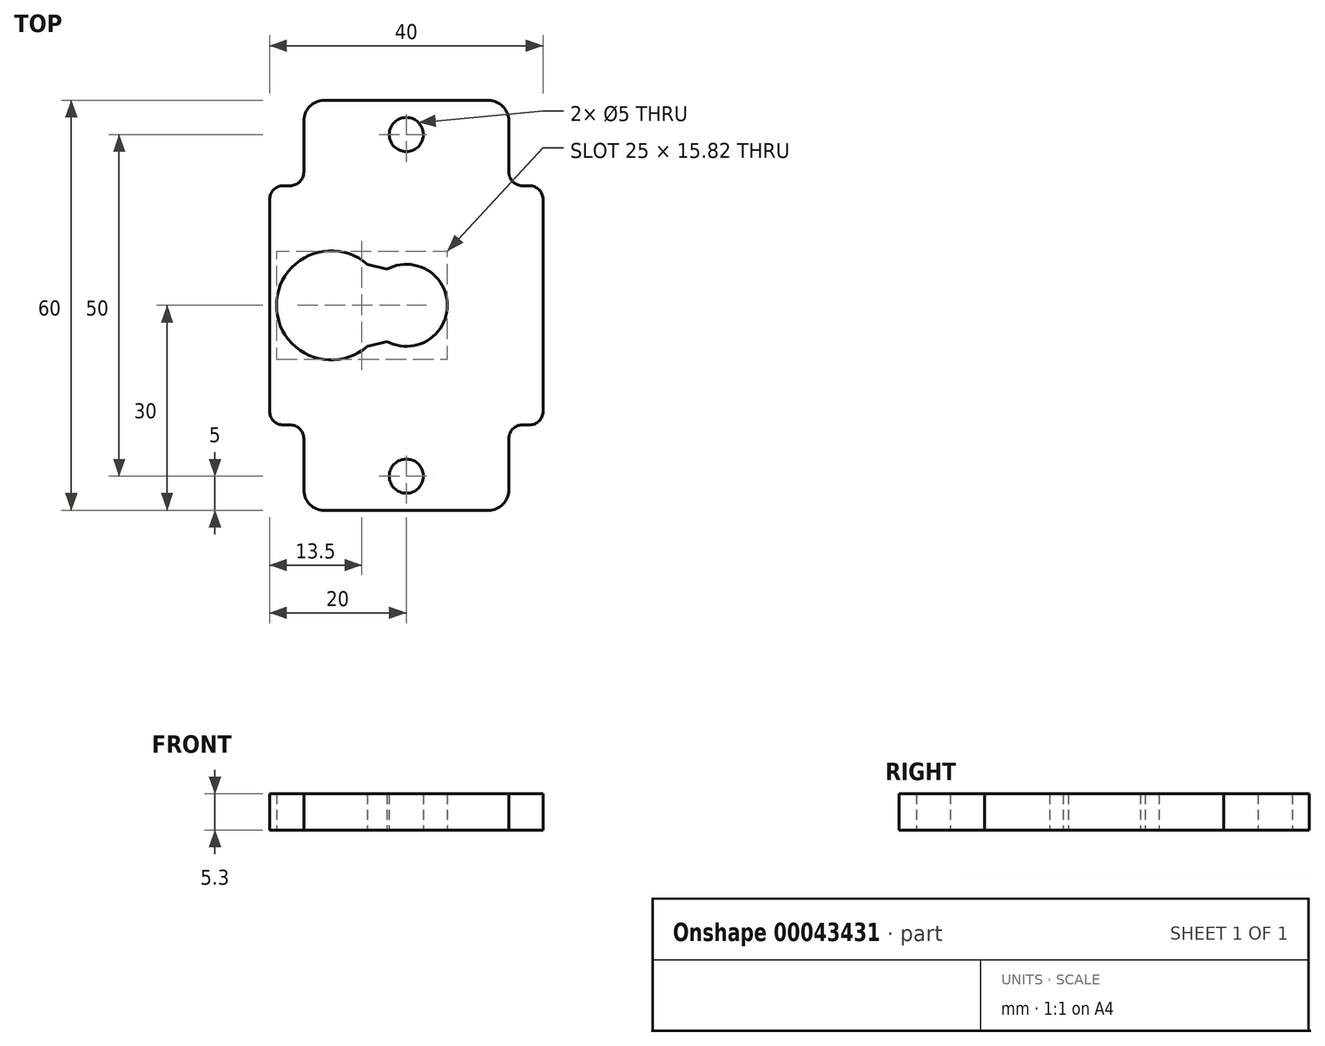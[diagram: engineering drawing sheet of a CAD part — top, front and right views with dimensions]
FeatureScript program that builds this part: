
annotation { "Feature Type Name" : "Feature", "Feature Type Description" : "" }
export const myFeature = defineFeature(function(context is Context, id is Id, definition is map)
    precondition{}
    {
        {
            var Q0;
            Q0=qCreatedBy(makeId("Top.planeOp"),FACE);
            var sketch = newSketch(context, id + "F0", { "sketchPlane" : qUnion([Q0])});
            skLineSegment(sketch, "E0.rect.bottom", {"start": v(12, -30) * mm, "end": v(-12, -30) * mm});
            skLineSegment(sketch, "E0.rect.top", {"start": v(12, 30) * mm, "end": v(-12, 30) * mm});
            skLineSegment(sketch, "E0.rect.left", {"start": v(15, -27) * mm, "end": v(15, -19.5) * mm});
            skLineSegment(sketch, "E0.rect.right", {"start": v(-15, -27) * mm, "end": v(-15, -19.5) * mm});
            skPoint(sketch, "E0.rect.middle", {"position": v(0, 0) * mm});
            skPoint(sketch, "E1.visualSharp", {"position": v(-15, 30) * mm});
            skArc(sketch, "E1.filletArc", {"start": v(-12, 30) * mm, "mid": v(-14.12, 29.12) * mm, "end": v(-15, 27) * mm});
            skPoint(sketch, "E2.visualSharp", {"position": v(15, 30) * mm});
            skArc(sketch, "E2.filletArc", {"start": v(15, 27) * mm, "mid": v(14.12, 29.12) * mm, "end": v(12, 30) * mm});
            skPoint(sketch, "E3.visualSharp", {"position": v(15, -30) * mm});
            skArc(sketch, "E3.filletArc", {"start": v(12, -30) * mm, "mid": v(14.12, -29.12) * mm, "end": v(15, -27) * mm});
            skPoint(sketch, "E4.visualSharp", {"position": v(-15, -30) * mm});
            skArc(sketch, "E4.filletArc", {"start": v(-15, -27) * mm, "mid": v(-14.12, -29.12) * mm, "end": v(-12, -30) * mm});
            skLineSegment(sketch, "E5.rect.bottom", {"start": v(18, 17.5) * mm, "end": v(17, 17.5) * mm});
            skLineSegment(sketch, "E5.rect.top", {"start": v(18, -17.5) * mm, "end": v(17, -17.5) * mm});
            skLineSegment(sketch, "E5.rect.left", {"start": v(20, 15.5) * mm, "end": v(20, -15.5) * mm});
            skLineSegment(sketch, "E5.rect.right", {"start": v(-20, 15.5) * mm, "end": v(-20, -15.5) * mm});
            skLineSegment(sketch, "E6.trimOffspring", {"start": v(-17, 17.5) * mm, "end": v(-18, 17.5) * mm});
            skLineSegment(sketch, "E7.trimOffspring", {"start": v(-15, 19.5) * mm, "end": v(-15, 27) * mm});
            skLineSegment(sketch, "E8.trimOffspring", {"start": v(15, 19.5) * mm, "end": v(15, 27) * mm});
            skLineSegment(sketch, "E9.trimOffspring", {"start": v(-17, -17.5) * mm, "end": v(-18, -17.5) * mm});
            skPoint(sketch, "E10.visualSharp", {"position": v(-15, 17.5) * mm});
            skArc(sketch, "E10.filletArc", {"start": v(-17, 17.5) * mm, "mid": v(-15.59, 18.09) * mm, "end": v(-15, 19.5) * mm});
            skPoint(sketch, "E11.visualSharp", {"position": v(-20, 17.5) * mm});
            skArc(sketch, "E11.filletArc", {"start": v(-18, 17.5) * mm, "mid": v(-19.41, 16.91) * mm, "end": v(-20, 15.5) * mm});
            skPoint(sketch, "E12.visualSharp", {"position": v(-20, -17.5) * mm});
            skArc(sketch, "E12.filletArc", {"start": v(-20, -15.5) * mm, "mid": v(-19.41, -16.91) * mm, "end": v(-18, -17.5) * mm});
            skPoint(sketch, "E13.visualSharp", {"position": v(-15, -17.5) * mm});
            skArc(sketch, "E13.filletArc", {"start": v(-15, -19.5) * mm, "mid": v(-15.59, -18.09) * mm, "end": v(-17, -17.5) * mm});
            skPoint(sketch, "E14.visualSharp", {"position": v(15, -17.5) * mm});
            skArc(sketch, "E14.filletArc", {"start": v(17, -17.5) * mm, "mid": v(15.59, -18.09) * mm, "end": v(15, -19.5) * mm});
            skPoint(sketch, "E15.visualSharp", {"position": v(20, -17.5) * mm});
            skArc(sketch, "E15.filletArc", {"start": v(18, -17.5) * mm, "mid": v(19.41, -16.91) * mm, "end": v(20, -15.5) * mm});
            skPoint(sketch, "E16.visualSharp", {"position": v(20, 17.5) * mm});
            skArc(sketch, "E16.filletArc", {"start": v(20, 15.5) * mm, "mid": v(19.41, 16.91) * mm, "end": v(18, 17.5) * mm});
            skPoint(sketch, "E17.visualSharp", {"position": v(15, 17.5) * mm});
            skArc(sketch, "E17.filletArc", {"start": v(15, 19.5) * mm, "mid": v(15.59, 18.09) * mm, "end": v(17, 17.5) * mm});
            skArc(sketch, "E18", {"start": v(-5.7, 6) * mm, "mid": v(-19, 0) * mm, "end": v(-5.7, -6) * mm});
            skLineSegment(sketch, "E19.bottom", {"start": v(0, 6) * mm, "end": v(-5.7, 6) * mm, "construction": true});
            skLineSegment(sketch, "E20.bottom", {"start": v(0, -6) * mm, "end": v(-5.7, -6) * mm, "construction": true});
            skCircle(sketch, "E21", {"center": v(0, 25) * mm, "radius": 2.5 * mm});
            skCircle(sketch, "E22", {"center": v(0, -25) * mm, "radius": 2.5 * mm});
            skLineSegment(sketch, "E23", {"start": v(-2.85, 6) * mm, "end": v(-2.85, -6) * mm, "construction": true});
            skArc(sketch, "E24", {"start": v(0, 6) * mm, "mid": v(-1.47, 5.82) * mm, "end": v(-2.85, 5.28) * mm});
            skArc(sketch, "E25", {"start": v(-2.85, -5.28) * mm, "mid": v(-1.47, -5.82) * mm, "end": v(0, -6) * mm});
            skArc(sketch, "E26", {"start": v(0, -6) * mm, "mid": v(6, 0) * mm, "end": v(0, 6) * mm});
            skLineSegment(sketch, "E27", {"start": v(-2.85, 5.28) * mm, "end": v(-5.7, 6) * mm});
            skLineSegment(sketch, "E28", {"start": v(-2.85, -5.28) * mm, "end": v(-5.7, -6) * mm});
            skSolve(sketch);
        }
        {
            var Q0;
            Q0=qSketchRegion(id+"F0",true);
            extrude(context, id + "F1", {"entities" : qUnion([Q0]), "depth" : 5.3 * mm});
        }
    });
